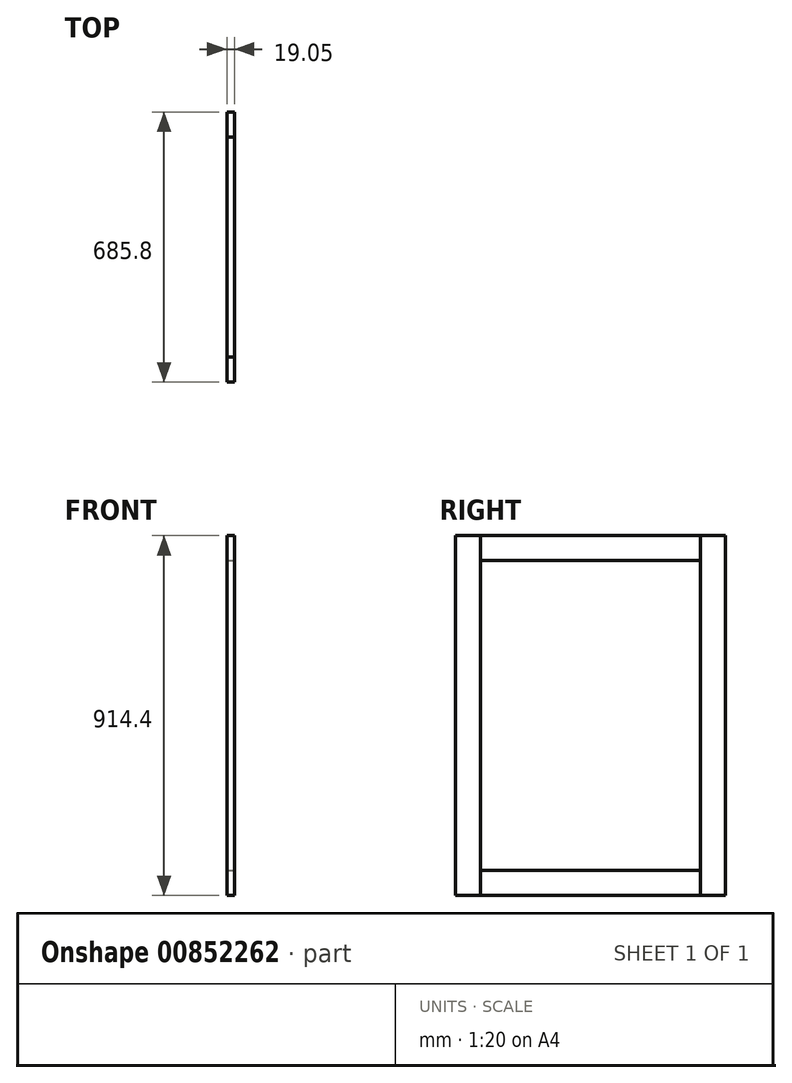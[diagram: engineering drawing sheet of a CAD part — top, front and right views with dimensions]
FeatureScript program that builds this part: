
annotation { "Feature Type Name" : "Feature", "Feature Type Description" : "" }
export const myFeature = defineFeature(function(context is Context, id is Id, definition is map)
    precondition{}
    {
        {
            var Q0;
            Q0=qCreatedBy(makeId("Right.planeOp"),FACE);
            var sketch = newSketch(context, id + "F0", { "sketchPlane" : qUnion([Q0])});
            skLineSegment(sketch, "E0.bottom", {"start": v(0, 0) * mm, "end": v(63.5, 0) * mm});
            skLineSegment(sketch, "E0.top", {"start": v(0, 914.4) * mm, "end": v(63.5, 914.4) * mm});
            skLineSegment(sketch, "E0.left", {"start": v(0, 0) * mm, "end": v(0, 914.4) * mm});
            skLineSegment(sketch, "E0.right", {"start": v(63.5, 0) * mm, "end": v(63.5, 914.4) * mm});
            skSolve(sketch);
        }
        {
            var Q0;
            Q0 = qSketchRegion(id + "F0", true);
            extrude(context, id + "F1", {"entities" : qUnion([Q0]), "depth" : 19.05 * mm, "offsetDistance" : 25.4 * mm});
        }
        {
            var Q0;
            Q0=qCreatedBy(makeId("Right.planeOp"),FACE);
            var sketch = newSketch(context, id + "F2", { "sketchPlane" : qUnion([Q0])});
            skLineSegment(sketch, "E1.bottom", {"start": v(622.3, 0) * mm, "end": v(685.8, 0) * mm});
            skLineSegment(sketch, "E1.top", {"start": v(622.3, 914.4) * mm, "end": v(685.8, 914.4) * mm});
            skLineSegment(sketch, "E1.left", {"start": v(622.3, 0) * mm, "end": v(622.3, 914.4) * mm});
            skLineSegment(sketch, "E1.right", {"start": v(685.8, 0) * mm, "end": v(685.8, 914.4) * mm});
            skSolve(sketch);
        }
        {
            var Q0;
            Q0 = qSketchRegion(id + "F2", true);
            extrude(context, id + "F3", {"entities" : qUnion([Q0]), "depth" : 19.05 * mm, "offsetDistance" : 25.4 * mm});
        }
        {
            var Q0;
            Q0=makeQuery(id+"F1.opExtrude","SWEPT_FACE",FACE,{"disambiguationData":[OSD([sQuery(id+"F0.wireOp",EDGE,"E0.right")])]});
            var sketch = newSketch(context, id + "F4", { "sketchPlane" : qUnion([Q0])});
            skLineSegment(sketch, "E2.bottom", {"start": v(-19.05, 914.4) * mm, "end": v(0, 914.4) * mm});
            skLineSegment(sketch, "E2.top", {"start": v(-19.05, 850.9) * mm, "end": v(0, 850.9) * mm});
            skLineSegment(sketch, "E2.left", {"start": v(-19.05, 914.4) * mm, "end": v(-19.05, 850.9) * mm});
            skLineSegment(sketch, "E2.right", {"start": v(0, 914.4) * mm, "end": v(0, 850.9) * mm});
            skSolve(sketch);
        }
        {
            var Q0;
            Q0 = qSketchRegion(id + "F4", true);
            var Q1;
            Q1=makeQuery(id+"F3.opExtrude","SWEPT_FACE",FACE,{"disambiguationData":[OSD([sQuery(id+"F2.wireOp",EDGE,"E1.left")])]});
            extrude(context, id + "F5", {"entities" : qUnion([Q0]), "endBound" : BoundingType.UP_TO_SURFACE, "depth" : 25.4 * mm, "endBoundEntityFace" : qUnion([Q1]), "offsetDistance" : 25.4 * mm});
        }
        {
            var Q0;
            Q0=makeQuery(id+"F1.opExtrude","SWEPT_FACE",FACE,{"disambiguationData":[OSD([sQuery(id+"F0.wireOp",EDGE,"E0.right")])]});
            var sketch = newSketch(context, id + "F6", { "sketchPlane" : qUnion([Q0])});
            skLineSegment(sketch, "E3.bottom", {"start": v(-19.05, 0) * mm, "end": v(0, 0) * mm});
            skLineSegment(sketch, "E3.top", {"start": v(-19.05, 63.5) * mm, "end": v(0, 63.5) * mm});
            skLineSegment(sketch, "E3.left", {"start": v(-19.05, 0) * mm, "end": v(-19.05, 63.5) * mm});
            skLineSegment(sketch, "E3.right", {"start": v(0, 0) * mm, "end": v(0, 63.5) * mm});
            skSolve(sketch);
        }
        {
            var Q0;
            Q0 = qSketchRegion(id + "F6", true);
            var Q1;
            Q1=makeQuery(id+"F3.opExtrude","SWEPT_FACE",FACE,{"disambiguationData":[OSD([sQuery(id+"F2.wireOp",EDGE,"E1.left")])]});
            extrude(context, id + "F7", {"entities" : qUnion([Q0]), "endBound" : BoundingType.UP_TO_SURFACE, "depth" : 25.4 * mm, "endBoundEntityFace" : qUnion([Q1]), "offsetDistance" : 25.4 * mm});
        }
    });
